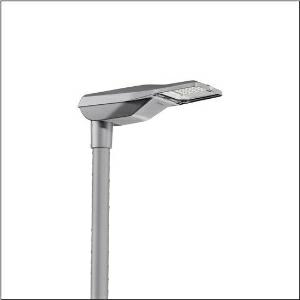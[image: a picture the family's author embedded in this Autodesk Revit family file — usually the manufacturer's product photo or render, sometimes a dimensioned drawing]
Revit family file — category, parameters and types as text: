
# Revit family: streetlight_sl_21_iq_micro___st1_5a_5xe1p41g08cb_60b9
name_source: partatom
category: Lighting Fixtures
units: mm (PartAtom-declared; Revit-internal decimal feet)

## family parameters
Cut with Voids When Loaded = No
Host = Face
Light Source = No
Part Type = Normal
Room Calculation Point = No
Round Connector Dimension = Use Diameter
Shared = No

## types (1)
- --- (1 x LED, 2930 lm, 19.4 W, 4000K)
    Apparent Load = 19 VA
    CIE Flux Codes = 22 53 95 100 100
    Color Rendering = 70
    Color Temperature = 4000K
    Default Elevation = 1800 mm
    Description = Streetlight SL 21 iQ micro, mast luminaire, primary light control with lens, of PMMA, primary optical cover: cover, of toughened safety glass, transparent, light distribution: ST1.5a, light emission: direct distribution, primary light characteristic: asymmetric, installation type: post-top, side-entry, LED, High Power LED, rated luminous flux: 2.930lm, luminous efficacy: 151lm/W, light colour: 740, colour temperature: 4000K, control gear: iQ Street-Remote, control: Street-Remote, Auto-Match, Temp-Guard, Lumen-Switch, Night-Set, Smart-Wire, Light-Fading, Desk-Remote (wireless, voltage-free reading and setting of iQ features in the workshop via application-optimized NFC function/RFID function), optimised constant luminous flux control (CLO 2.0), pre-setting: linear dimming characteristic, mains connection: 220..240V, AC, 50/60Hz, start of lifetime: 19W, end of service life: 20W, reduction: 10W, luminaire housing, of diecast aluminium, powder-coated, Siteco® metallic grey (DB 702S), corrosivity category C5 mid according to DIN EN ISO 12944, please order mast flange separately, inclination adjustable: 0°, 5°, 10°, 15°, sealing non-destructively replaceable, multi-level sealing system, length: 528mm, width: 235mm, height: 110mm, mast flange for spigot size: 42mm (side-entry): 5XC10008XM4, 60/48mm (side-entry/post-top): 5XC10108XM2, 76/60mm (side-entry/post-top): 5XC10108XM1, protection rating (complete): IP66, insulation class (complete): insulation class II (safety insulation), certification: CE, ENEC, ENEC+, VDE, impact resistance: IK10, permissible operating ambient temperature for outdoor applications: -40..+50°C, standard-compliant lighting for roads and squares, packaging unit: 1 piece

Light Distribution: ST1.5a
    Height = 110 mm
    Lamp = 1 x LED
    Lamp Light Flux = 2930 lm
    Lamp Power = 19.4 W
    Lamp count = 1
    Length = 528 mm
    Luminous efficacy = 151 lm/W
    Manufacturer = Siteco
    ModVariant = No
    Model = 5XE1P41G08CB
    Number of Poles = 1
    OnlyDefault = Yes
    Power Factor = 1
    Product Name = Streetlight SL 21 iQ micro | ST1.5a
    Product group = mast luminaire | pylon top
    ProductGroupID = 6100
    Protection Class = Protection class II
    Protection Degree = IP 66
    RLX_Detail_Level = 1
    RLX_Emergency_Light_Flux = 0 lm
    RLX_Emergency_Type = 0
    RLX_Emergency_Type_DB = No
    RlxData = <blob elided: 102373 chars, md5=ce46b89b>
    Socket = socket
    Standby Power = 0 W
    System Light Flux = 2930 lm
    System Power = 19 W
    Type Comments = factory setting: luminous flux: 100 % | dim-lin: 254 | 387 mA
    Type Image = l_1006881.jpg
    URL = http://relux.com
    VarID = @adj_138000
    Voltage = 0 V
    Weight = 0.00 kg
    Width = 235 mm

## geometry (parser evidence)
native form markers: Blend x4, Sweep x10
no freeform markers — native parametric forms only
